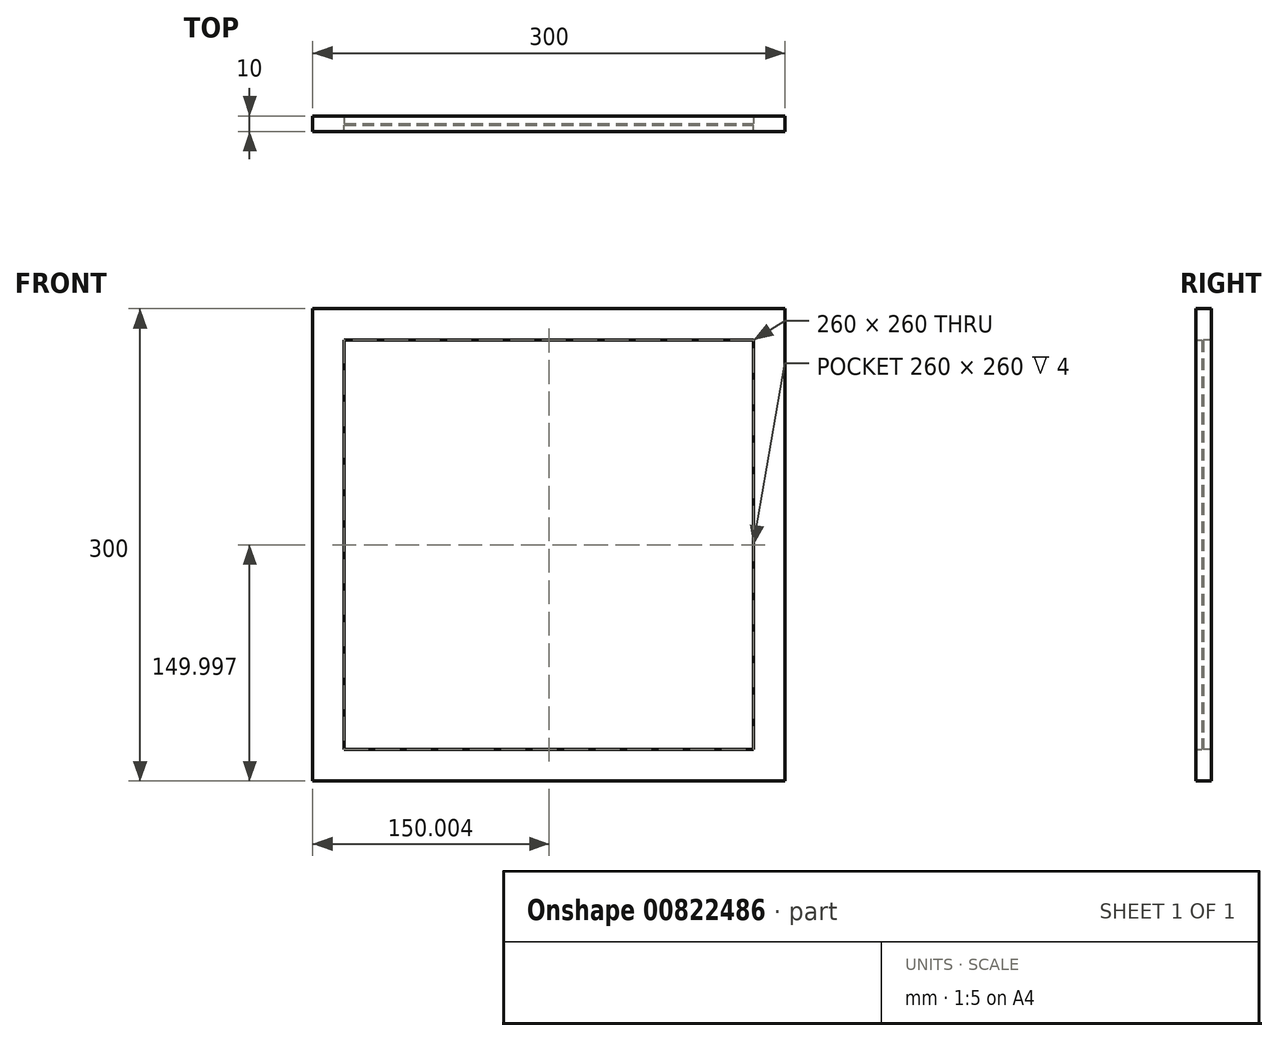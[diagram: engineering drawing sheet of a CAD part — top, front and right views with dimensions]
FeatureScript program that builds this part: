
annotation { "Feature Type Name" : "Feature", "Feature Type Description" : "" }
export const myFeature = defineFeature(function(context is Context, id is Id, definition is map)
    precondition{}
    {
        {
            var Q0;
            Q0=qCreatedBy(makeId("Front.planeOp"),FACE);
            var sketch = newSketch(context, id + "F0", { "sketchPlane" : qUnion([Q0])});
            skLineSegment(sketch, "E0.bottom", {"start": v(-221.64, 94.4) * mm, "end": v(78.36, 94.4) * mm});
            skLineSegment(sketch, "E0.top", {"start": v(-221.64, -205.6) * mm, "end": v(78.36, -205.6) * mm});
            skLineSegment(sketch, "E0.left", {"start": v(-221.64, 94.4) * mm, "end": v(-221.64, -205.6) * mm});
            skLineSegment(sketch, "E0.right", {"start": v(78.36, 94.4) * mm, "end": v(78.36, -205.6) * mm});
            skLineSegment(sketch, "E1", {"start": v(-201.64, 94.4) * mm, "end": v(-201.64, -205.6) * mm});
            skLineSegment(sketch, "E2", {"start": v(58.36, 94.4) * mm, "end": v(58.36, -205.6) * mm});
            skLineSegment(sketch, "E3", {"start": v(-221.64, 74.4) * mm, "end": v(78.36, 74.4) * mm});
            skLineSegment(sketch, "E4", {"start": v(-221.64, -185.6) * mm, "end": v(78.36, -185.6) * mm});
            skSolve(sketch);
        }
        {
            var Q0;
            {var subQ0=sQuery(id+"F0.wireOp",EDGE,"E3");var subQ1=sQuery(id+"F0.wireOp",EDGE,"E1");var subQ2=makeQuery(id+"F0.imprint","INTERSECT",VERTEX,{"derivedFrom":[subQ1,subQ0]});Q0=makeQuery(id+"F0.imprint","IMPRINT",FACE,{"disambiguationData":[TD([[makeQuery(id+"F0.imprint","IMPRINT",EDGE,{"disambiguationData":[TD([[subQ2,-1.0]])],"derivedFrom":subQ1}),1.0]])]});}
            extrude(context, id + "F1", {"entities" : qUnion([Q0]), "depth" : 1 * mm, "offsetDistance" : 25.4 * mm});
        }
        {
            var Q0;
            {var subQ0=sQuery(id+"F0.wireOp",EDGE,"E1");var subQ1=sQuery(id+"F0.wireOp",EDGE,"E0.bottom");var subQ2=makeQuery(id+"F0.imprint","INTERSECT",VERTEX,{"derivedFrom":[subQ1,subQ0]});Q0=makeQuery(id+"F0.imprint","IMPRINT",FACE,{"disambiguationData":[TD([[makeQuery(id+"F0.imprint","IMPRINT",EDGE,{"disambiguationData":[TD([[subQ2,-1.0]])],"derivedFrom":subQ1}),-1.0]])]});}
            var Q1;
            {var subQ0=sQuery(id+"F0.wireOp",EDGE,"E0.right");var subQ1=sQuery(id+"F0.wireOp",EDGE,"E0.bottom");var subQ2=makeQuery(id+"F0.imprint","INTERSECT",VERTEX,{"derivedFrom":[subQ1,subQ0]});Q1=makeQuery(id+"F0.imprint","IMPRINT",FACE,{"disambiguationData":[TD([[makeQuery(id+"F0.imprint","IMPRINT",EDGE,{"disambiguationData":[TD([[subQ2,1.0]])],"derivedFrom":subQ1}),-1.0]])]});}
            var Q2;
            {var subQ0=sQuery(id+"F0.wireOp",EDGE,"E3");var subQ1=sQuery(id+"F0.wireOp",EDGE,"E0.right");var subQ2=makeQuery(id+"F0.imprint","INTERSECT",VERTEX,{"derivedFrom":[subQ1,subQ0]});Q2=makeQuery(id+"F0.imprint","IMPRINT",FACE,{"disambiguationData":[TD([[makeQuery(id+"F0.imprint","IMPRINT",EDGE,{"disambiguationData":[TD([[subQ2,-1.0]])],"derivedFrom":subQ1}),-1.0]])]});}
            var Q3;
            {var subQ0=sQuery(id+"F0.wireOp",EDGE,"E0.right");var subQ1=sQuery(id+"F0.wireOp",EDGE,"E0.top");var subQ2=makeQuery(id+"F0.imprint","INTERSECT",VERTEX,{"derivedFrom":[subQ1,subQ0]});Q3=makeQuery(id+"F0.imprint","IMPRINT",FACE,{"disambiguationData":[TD([[makeQuery(id+"F0.imprint","IMPRINT",EDGE,{"disambiguationData":[TD([[subQ2,1.0]])],"derivedFrom":subQ1}),1.0]])]});}
            var Q4;
            {var subQ0=sQuery(id+"F0.wireOp",EDGE,"E1");var subQ1=sQuery(id+"F0.wireOp",EDGE,"E0.top");var subQ2=makeQuery(id+"F0.imprint","INTERSECT",VERTEX,{"derivedFrom":[subQ1,subQ0]});Q4=makeQuery(id+"F0.imprint","IMPRINT",FACE,{"disambiguationData":[TD([[makeQuery(id+"F0.imprint","IMPRINT",EDGE,{"disambiguationData":[TD([[subQ2,-1.0]])],"derivedFrom":subQ1}),1.0]])]});}
            var Q5;
            {var subQ0=sQuery(id+"F0.wireOp",EDGE,"E0.left");var subQ1=sQuery(id+"F0.wireOp",EDGE,"E0.top");var subQ2=makeQuery(id+"F0.imprint","INTERSECT",VERTEX,{"derivedFrom":[subQ1,subQ0]});Q5=makeQuery(id+"F0.imprint","IMPRINT",FACE,{"disambiguationData":[TD([[makeQuery(id+"F0.imprint","IMPRINT",EDGE,{"disambiguationData":[TD([[subQ2,-1.0]])],"derivedFrom":subQ1}),1.0]])]});}
            var Q6;
            {var subQ0=sQuery(id+"F0.wireOp",EDGE,"E3");var subQ1=sQuery(id+"F0.wireOp",EDGE,"E0.left");var subQ2=makeQuery(id+"F0.imprint","INTERSECT",VERTEX,{"derivedFrom":[subQ1,subQ0]});Q6=makeQuery(id+"F0.imprint","IMPRINT",FACE,{"disambiguationData":[TD([[makeQuery(id+"F0.imprint","IMPRINT",EDGE,{"disambiguationData":[TD([[subQ2,-1.0]])],"derivedFrom":subQ1}),1.0]])]});}
            var Q7;
            {var subQ0=sQuery(id+"F0.wireOp",EDGE,"E0.left");var subQ1=sQuery(id+"F0.wireOp",EDGE,"E0.bottom");var subQ2=makeQuery(id+"F0.imprint","INTERSECT",VERTEX,{"derivedFrom":[subQ1,subQ0]});Q7=makeQuery(id+"F0.imprint","IMPRINT",FACE,{"disambiguationData":[TD([[makeQuery(id+"F0.imprint","IMPRINT",EDGE,{"disambiguationData":[TD([[subQ2,-1.0]])],"derivedFrom":subQ1}),-1.0]])]});}
            extrude(context, id + "F2", {"entities" : qUnion([Q0, Q1, Q2, Q3, Q4, Q5, Q6, Q7]), "operationType" : NewBodyOperationType.ADD, "depth" : 5 * mm, "offsetDistance" : 25.4 * mm});
        }
        {
            var Q0;
            {var subQ0=sQuery(id+"F0.wireOp",EDGE,"E1");var subQ1=sQuery(id+"F0.wireOp",EDGE,"E0.bottom");var subQ2=makeQuery(id+"F0.imprint","INTERSECT",VERTEX,{"derivedFrom":[subQ1,subQ0]});Q0=makeQuery(id+"F0.imprint","IMPRINT",FACE,{"disambiguationData":[TD([[makeQuery(id+"F0.imprint","IMPRINT",EDGE,{"disambiguationData":[TD([[subQ2,-1.0]])],"derivedFrom":subQ1}),-1.0]])]});}
            var Q1;
            {var subQ0=sQuery(id+"F0.wireOp",EDGE,"E0.right");var subQ1=sQuery(id+"F0.wireOp",EDGE,"E0.bottom");var subQ2=makeQuery(id+"F0.imprint","INTERSECT",VERTEX,{"derivedFrom":[subQ1,subQ0]});Q1=makeQuery(id+"F0.imprint","IMPRINT",FACE,{"disambiguationData":[TD([[makeQuery(id+"F0.imprint","IMPRINT",EDGE,{"disambiguationData":[TD([[subQ2,1.0]])],"derivedFrom":subQ1}),-1.0]])]});}
            var Q2;
            {var subQ0=sQuery(id+"F0.wireOp",EDGE,"E3");var subQ1=sQuery(id+"F0.wireOp",EDGE,"E0.right");var subQ2=makeQuery(id+"F0.imprint","INTERSECT",VERTEX,{"derivedFrom":[subQ1,subQ0]});Q2=makeQuery(id+"F0.imprint","IMPRINT",FACE,{"disambiguationData":[TD([[makeQuery(id+"F0.imprint","IMPRINT",EDGE,{"disambiguationData":[TD([[subQ2,-1.0]])],"derivedFrom":subQ1}),-1.0]])]});}
            var Q3;
            {var subQ0=sQuery(id+"F0.wireOp",EDGE,"E0.right");var subQ1=sQuery(id+"F0.wireOp",EDGE,"E0.top");var subQ2=makeQuery(id+"F0.imprint","INTERSECT",VERTEX,{"derivedFrom":[subQ1,subQ0]});Q3=makeQuery(id+"F0.imprint","IMPRINT",FACE,{"disambiguationData":[TD([[makeQuery(id+"F0.imprint","IMPRINT",EDGE,{"disambiguationData":[TD([[subQ2,1.0]])],"derivedFrom":subQ1}),1.0]])]});}
            var Q4;
            {var subQ0=sQuery(id+"F0.wireOp",EDGE,"E1");var subQ1=sQuery(id+"F0.wireOp",EDGE,"E0.top");var subQ2=makeQuery(id+"F0.imprint","INTERSECT",VERTEX,{"derivedFrom":[subQ1,subQ0]});Q4=makeQuery(id+"F0.imprint","IMPRINT",FACE,{"disambiguationData":[TD([[makeQuery(id+"F0.imprint","IMPRINT",EDGE,{"disambiguationData":[TD([[subQ2,-1.0]])],"derivedFrom":subQ1}),1.0]])]});}
            var Q5;
            {var subQ0=sQuery(id+"F0.wireOp",EDGE,"E0.left");var subQ1=sQuery(id+"F0.wireOp",EDGE,"E0.top");var subQ2=makeQuery(id+"F0.imprint","INTERSECT",VERTEX,{"derivedFrom":[subQ1,subQ0]});Q5=makeQuery(id+"F0.imprint","IMPRINT",FACE,{"disambiguationData":[TD([[makeQuery(id+"F0.imprint","IMPRINT",EDGE,{"disambiguationData":[TD([[subQ2,-1.0]])],"derivedFrom":subQ1}),1.0]])]});}
            var Q6;
            {var subQ0=sQuery(id+"F0.wireOp",EDGE,"E3");var subQ1=sQuery(id+"F0.wireOp",EDGE,"E0.left");var subQ2=makeQuery(id+"F0.imprint","INTERSECT",VERTEX,{"derivedFrom":[subQ1,subQ0]});Q6=makeQuery(id+"F0.imprint","IMPRINT",FACE,{"disambiguationData":[TD([[makeQuery(id+"F0.imprint","IMPRINT",EDGE,{"disambiguationData":[TD([[subQ2,-1.0]])],"derivedFrom":subQ1}),1.0]])]});}
            var Q7;
            {var subQ0=sQuery(id+"F0.wireOp",EDGE,"E0.left");var subQ1=sQuery(id+"F0.wireOp",EDGE,"E0.bottom");var subQ2=makeQuery(id+"F0.imprint","INTERSECT",VERTEX,{"derivedFrom":[subQ1,subQ0]});Q7=makeQuery(id+"F0.imprint","IMPRINT",FACE,{"disambiguationData":[TD([[makeQuery(id+"F0.imprint","IMPRINT",EDGE,{"disambiguationData":[TD([[subQ2,-1.0]])],"derivedFrom":subQ1}),-1.0]])]});}
            extrude(context, id + "F3", {"entities" : qUnion([Q0, Q1, Q2, Q3, Q4, Q5, Q6, Q7]), "operationType" : NewBodyOperationType.ADD, "depth" : -5 * mm, "offsetDistance" : 25.4 * mm});
        }
    });
